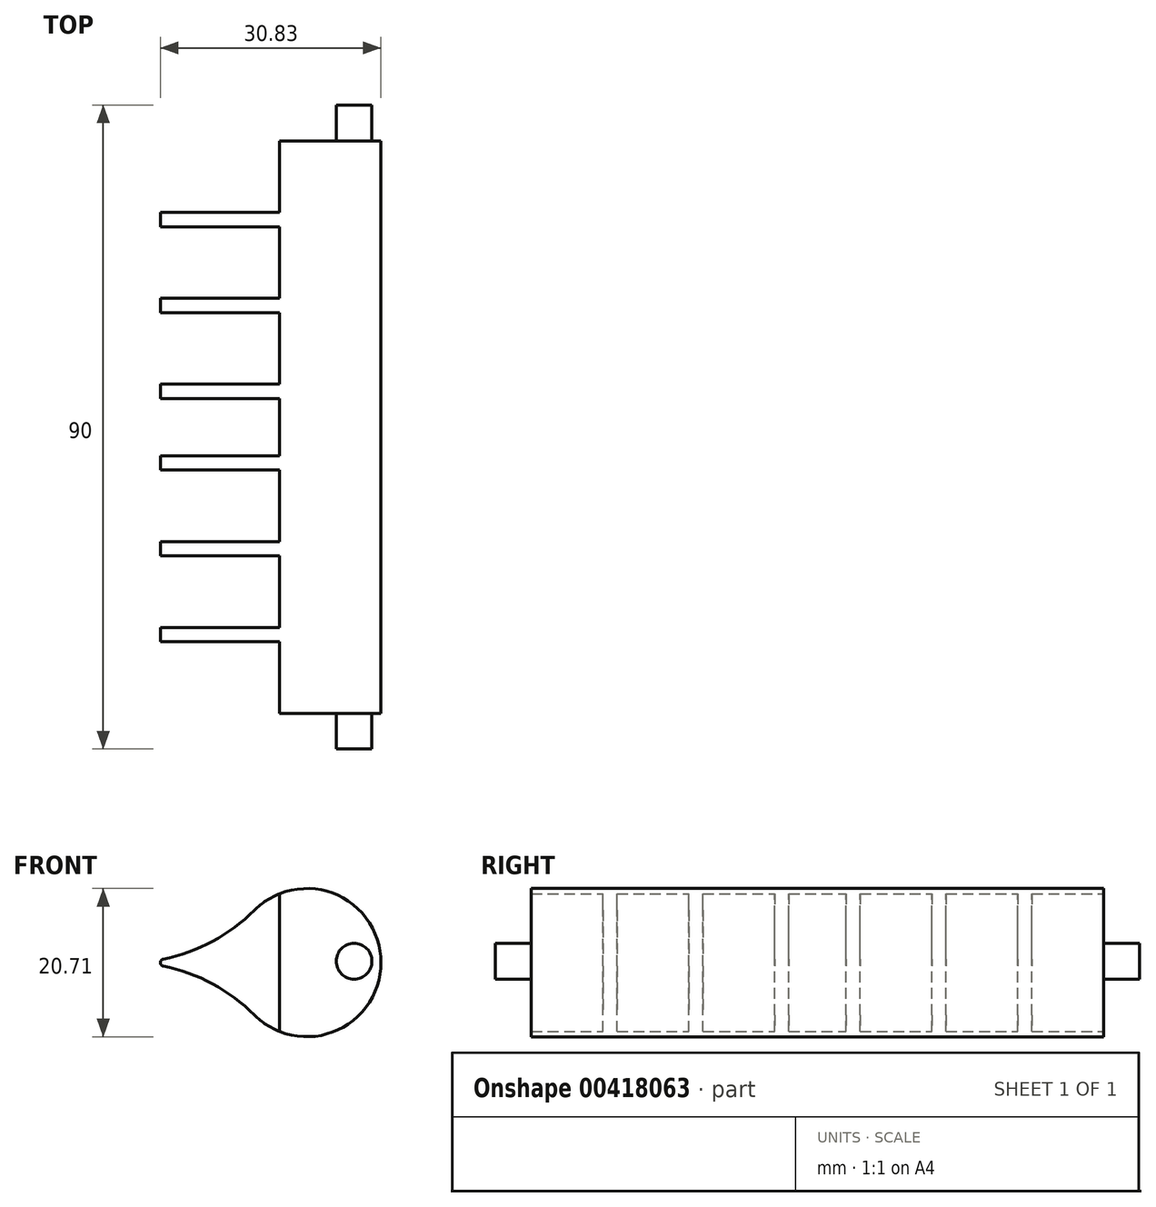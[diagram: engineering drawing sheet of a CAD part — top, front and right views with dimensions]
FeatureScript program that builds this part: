
annotation { "Feature Type Name" : "Feature", "Feature Type Description" : "" }
export const myFeature = defineFeature(function(context is Context, id is Id, definition is map)
    precondition{}
    {
        {
            var Q0;
            Q0=qCreatedBy(makeId("Front.planeOp"),FACE);
            var sketch = newSketch(context, id + "F0", { "sketchPlane" : qUnion([Q0])});
            skArc(sketch, "E0", {"start": v(-3.7, 0.3) * mm, "mid": v(3.19, 2.77) * mm, "end": v(9.06, 7.13) * mm});
            skArc(sketch, "E1", {"start": v(9.06, -7.51) * mm, "mid": v(3.19, -3.16) * mm, "end": v(-3.7, -0.68) * mm});
            skArc(sketch, "E2", {"start": v(9.06, -7.51) * mm, "mid": v(26.74, -0.2) * mm, "end": v(9.06, 7.13) * mm});
            skPoint(sketch, "E3.visualSharp", {"position": v(-8.62, -0.2) * mm});
            skArc(sketch, "E3.filletArc", {"start": v(-3.7, 0.3) * mm, "mid": v(-4.1, -0.2) * mm, "end": v(-3.7, -0.68) * mm});
            skSolve(sketch);
        }
        {
            var Q0;
            Q0 = qSketchRegion(id + "F0", true);
            extrude(context, id + "F1", {"entities" : qUnion([Q0]), "depth" : 80 * mm, "offsetDistance" : 25 * mm});
        }
        {
            var Q0;
            Q0=qCreatedBy(makeId("Top.planeOp"),FACE);
            var sketch = newSketch(context, id + "F2", { "sketchPlane" : qUnion([Q0])});
            skLineSegment(sketch, "E4", {"start": v(-6.23, -10) * mm, "end": v(12.59, -10) * mm});
            skLineSegment(sketch, "E5", {"start": v(12.59, 2.99) * mm, "end": v(12.59, -10) * mm});
            skLineSegment(sketch, "E6", {"start": v(-6.23, -12) * mm, "end": v(12.59, -12) * mm});
            skLineSegment(sketch, "E7", {"start": v(-6.23, -22) * mm, "end": v(12.59, -22) * mm});
            skLineSegment(sketch, "E8", {"start": v(-6.23, -24) * mm, "end": v(12.59, -24) * mm});
            skLineSegment(sketch, "E9", {"start": v(-6.23, -34) * mm, "end": v(12.59, -34) * mm});
            skLineSegment(sketch, "E10", {"start": v(-6.23, -36) * mm, "end": v(12.59, -36) * mm});
            skLineSegment(sketch, "E11", {"start": v(-5.7, -44) * mm, "end": v(12.59, -44) * mm});
            skLineSegment(sketch, "E12", {"start": v(-5.7, -46) * mm, "end": v(12.59, -46) * mm});
            skLineSegment(sketch, "E13", {"start": v(12.59, -70) * mm, "end": v(-6.23, -70) * mm});
            skLineSegment(sketch, "E14", {"start": v(12.59, -68) * mm, "end": v(-6.23, -68) * mm});
            skLineSegment(sketch, "E15", {"start": v(12.59, -58) * mm, "end": v(-6.23, -58) * mm});
            skLineSegment(sketch, "E16", {"start": v(12.59, -56) * mm, "end": v(-6.23, -56) * mm});
            skLineSegment(sketch, "E17", {"start": v(12.59, 2.99) * mm, "end": v(-20.3, 2.99) * mm});
            skLineSegment(sketch, "E18", {"start": v(-20.3, 2.99) * mm, "end": v(-20.3, -84.1) * mm});
            skLineSegment(sketch, "E19", {"start": v(-20.3, -84.1) * mm, "end": v(12.59, -84.75) * mm});
            skLineSegment(sketch, "E20", {"start": v(-6.23, -10) * mm, "end": v(-6.23, -12) * mm});
            skLineSegment(sketch, "E21.trimOffspring", {"start": v(-6.23, -68) * mm, "end": v(-6.23, -70) * mm});
            skPoint(sketch, "E22.orphan", {"position": v(-8.17, -58) * mm});
            skPoint(sketch, "E23.orphan", {"position": v(-8.17, -56) * mm});
            skLineSegment(sketch, "E24.trimOffspring", {"start": v(-6.23, -56) * mm, "end": v(-6.23, -58) * mm});
            skLineSegment(sketch, "E25.trimOffspring", {"start": v(-6.23, -34) * mm, "end": v(-6.23, -36) * mm});
            skPoint(sketch, "E26.orphan", {"position": v(-8.06, -12) * mm});
            skPoint(sketch, "E27.orphan", {"position": v(-8.06, -10) * mm});
            skLineSegment(sketch, "E28.trimOffspring", {"start": v(-6.23, -22) * mm, "end": v(-6.23, -24) * mm});
            skLineSegment(sketch, "E29.trimOffspring", {"start": v(12.59, -24) * mm, "end": v(12.59, -34) * mm});
            skLineSegment(sketch, "E30.trimOffspring", {"start": v(12.59, -36) * mm, "end": v(12.59, -44) * mm});
            skLineSegment(sketch, "E31.trimOffspring", {"start": v(12.59, -46) * mm, "end": v(12.59, -56) * mm});
            skLineSegment(sketch, "E32.trimOffspring", {"start": v(12.59, -58) * mm, "end": v(12.59, -68) * mm});
            skLineSegment(sketch, "E33.trimOffspring", {"start": v(12.59, -70) * mm, "end": v(12.59, -84.75) * mm});
            skLineSegment(sketch, "E34", {"start": v(12.59, -12) * mm, "end": v(12.59, -22) * mm});
            skLineSegment(sketch, "E35", {"start": v(-5.7, -44) * mm, "end": v(-5.7, -46) * mm});
            skSolve(sketch);
        }
        {
            var Q0;
            Q0 = qSketchRegion(id + "F2", true);
            extrude(context, id + "F3", {"entities" : qUnion([Q0]), "operationType" : NewBodyOperationType.REMOVE, "endBound" : BoundingType.SYMMETRIC, "oppositeDirection" : true, "depth" : 25 * mm, "offsetDistance" : 25 * mm});
        }
        {
            var Q0;
            Q0=makeQuery(id+"F1.opExtrude","CAP_FACE",FACE,{"disambiguationData":[OSD([sQuery(id+"F0.wireOp",EDGE,"E0"),sQuery(id+"F0.wireOp",EDGE,"E1"),sQuery(id+"F0.wireOp",EDGE,"E2"),sQuery(id+"F0.wireOp",EDGE,"E3.filletArc"),sQuery(id+"F0.wireOp",EDGE,"AvYLteHY-9WNd-3iUX-Dhs0-umPzgOFaGaEr")])],"isStart":false});
            var sketch = newSketch(context, id + "F4", { "sketchPlane" : qUnion([Q0])});
            skCircle(sketch, "E36", {"center": v(22.98, 0) * mm, "radius": 2.5 * mm});
            skSolve(sketch);
        }
        {
            var Q0;
            Q0 = qSketchRegion(id + "F4", true);
            extrude(context, id + "F5", {"entities" : qUnion([Q0]), "operationType" : NewBodyOperationType.ADD, "depth" : 5 * mm, "offsetDistance" : 25 * mm});
        }
        {
            var Q0;
            Q0=makeQuery(id+"F1.opExtrude","CAP_FACE",FACE,{"disambiguationData":[OSD([sQuery(id+"F0.wireOp",EDGE,"E0"),sQuery(id+"F0.wireOp",EDGE,"E1"),sQuery(id+"F0.wireOp",EDGE,"E2"),sQuery(id+"F0.wireOp",EDGE,"E3.filletArc"),sQuery(id+"F0.wireOp",EDGE,"AvYLteHY-9WNd-3iUX-Dhs0-umPzgOFaGaEr")])],"isStart":true});
            var sketch = newSketch(context, id + "F6", { "sketchPlane" : qUnion([Q0])});
            skCircle(sketch, "E37", {"center": v(-22.98, 0) * mm, "radius": 2.5 * mm});
            skSolve(sketch);
        }
        {
            var Q0;
            Q0 = qSketchRegion(id + "F6", true);
            extrude(context, id + "F7", {"entities" : qUnion([Q0]), "operationType" : NewBodyOperationType.ADD, "depth" : 5 * mm, "offsetDistance" : 25 * mm});
        }
    });
